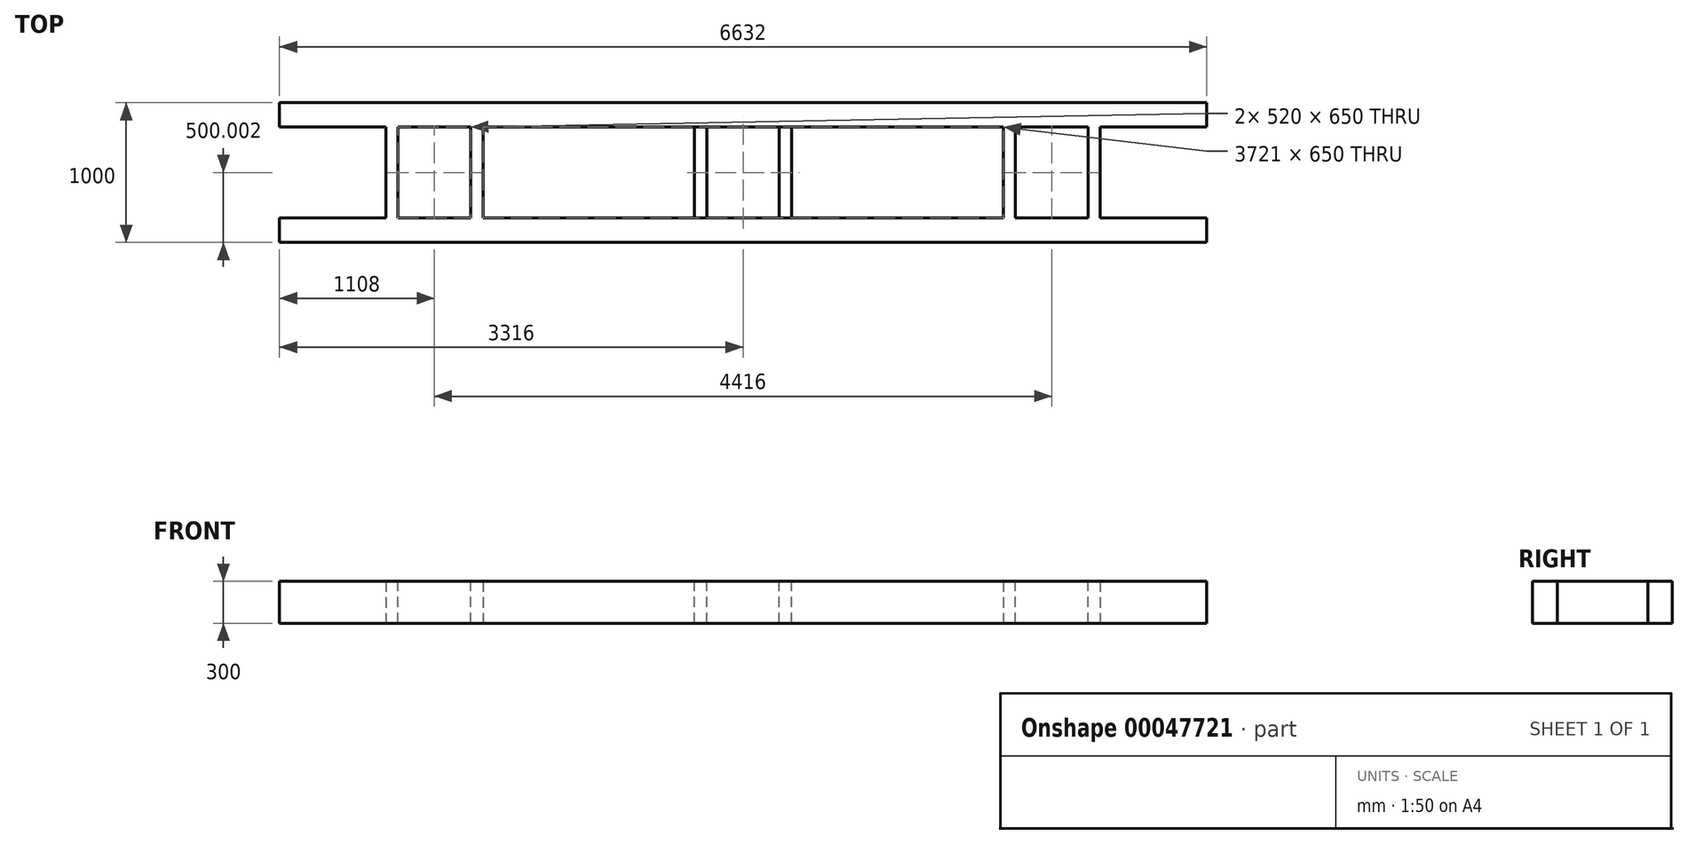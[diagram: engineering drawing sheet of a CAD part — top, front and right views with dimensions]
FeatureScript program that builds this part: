
annotation { "Feature Type Name" : "Feature", "Feature Type Description" : "" }
export const myFeature = defineFeature(function(context is Context, id is Id, definition is map)
    precondition{}
    {
        {
            var Q0;
            Q0=qCreatedBy(makeId("Top.planeOp"),FACE);
            var sketch = newSketch(context, id + "F0", { "sketchPlane" : qUnion([Q0])});
            skLineSegment(sketch, "E0.bottom", {"start": v(-3316.66, -990.23) * mm, "end": v(3315.34, -990.23) * mm});
            skLineSegment(sketch, "E0.top", {"start": v(-3316.66, -1165.23) * mm, "end": v(3315.34, -1165.23) * mm});
            skLineSegment(sketch, "E0.left", {"start": v(-3316.66, -990.23) * mm, "end": v(-3316.66, -1165.23) * mm});
            skLineSegment(sketch, "E0.right", {"start": v(3315.34, -990.23) * mm, "end": v(3315.34, -1165.23) * mm});
            skLineSegment(sketch, "E1", {"start": v(-3316.66, -990.23) * mm, "end": v(-3316.66, -340.23) * mm, "construction": true});
            skLineSegment(sketch, "E2.bottom", {"start": v(-3316.66, -340.23) * mm, "end": v(3315.34, -340.23) * mm});
            skLineSegment(sketch, "E2.top", {"start": v(-3316.66, -165.23) * mm, "end": v(3315.34, -165.23) * mm});
            skLineSegment(sketch, "E2.left", {"start": v(-3316.66, -340.23) * mm, "end": v(-3316.66, -165.23) * mm});
            skLineSegment(sketch, "E2.right", {"start": v(3315.34, -340.23) * mm, "end": v(3315.34, -165.23) * mm});
            skLineSegment(sketch, "E3.bottom", {"start": v(-3316.66, -340.23) * mm, "end": v(-2556.16, -340.23) * mm, "construction": true});
            skLineSegment(sketch, "E3.top", {"start": v(-3316.66, -990.23) * mm, "end": v(-2556.16, -990.23) * mm, "construction": true});
            skLineSegment(sketch, "E3.left", {"start": v(-3316.66, -340.23) * mm, "end": v(-3316.66, -990.23) * mm, "construction": true});
            skLineSegment(sketch, "E3.right", {"start": v(-2556.16, -340.23) * mm, "end": v(-2556.16, -990.23) * mm, "construction": true});
            skLineSegment(sketch, "E4.bottom", {"start": v(-2556.16, -340.23) * mm, "end": v(-1861.16, -340.23) * mm});
            skLineSegment(sketch, "E4.top", {"start": v(-2556.16, -990.23) * mm, "end": v(-1861.16, -990.23) * mm});
            skLineSegment(sketch, "E4.left", {"start": v(-2556.16, -340.23) * mm, "end": v(-2556.16, -990.23) * mm});
            skLineSegment(sketch, "E4.right", {"start": v(-1861.16, -340.23) * mm, "end": v(-1861.16, -990.23) * mm});
            skLineSegment(sketch, "E5.bottom", {"start": v(-2556.16, -340.23) * mm, "end": v(-348.16, -340.23) * mm, "construction": true});
            skLineSegment(sketch, "E5.top", {"start": v(-2556.16, -990.23) * mm, "end": v(-348.16, -990.23) * mm, "construction": true});
            skLineSegment(sketch, "E5.right", {"start": v(-348.16, -340.23) * mm, "end": v(-348.16, -990.23) * mm, "construction": true});
            skLineSegment(sketch, "E6.bottom", {"start": v(-348.16, -340.23) * mm, "end": v(346.84, -340.23) * mm});
            skLineSegment(sketch, "E6.top", {"start": v(-348.16, -990.23) * mm, "end": v(346.84, -990.23) * mm});
            skLineSegment(sketch, "E6.left", {"start": v(-348.16, -340.23) * mm, "end": v(-348.16, -990.23) * mm});
            skLineSegment(sketch, "E6.right", {"start": v(346.84, -340.23) * mm, "end": v(346.84, -990.23) * mm});
            skLineSegment(sketch, "E7.bottom", {"start": v(-348.16, -340.23) * mm, "end": v(1859.84, -340.23) * mm, "construction": true});
            skLineSegment(sketch, "E7.top", {"start": v(-348.16, -990.23) * mm, "end": v(1859.84, -990.23) * mm, "construction": true});
            skLineSegment(sketch, "E7.right", {"start": v(1859.84, -340.23) * mm, "end": v(1859.84, -990.23) * mm, "construction": true});
            skLineSegment(sketch, "E8.bottom", {"start": v(1859.84, -340.23) * mm, "end": v(2554.84, -340.23) * mm});
            skLineSegment(sketch, "E8.top", {"start": v(1859.84, -990.23) * mm, "end": v(2554.84, -990.23) * mm});
            skLineSegment(sketch, "E8.left", {"start": v(1859.84, -340.23) * mm, "end": v(1859.84, -990.23) * mm});
            skLineSegment(sketch, "E8.right", {"start": v(2554.84, -340.23) * mm, "end": v(2554.84, -990.23) * mm});
            skSolve(sketch);
        }
        {
            var Q0;
            Q0 = qSketchRegion(id + "F0", true);
            extrude(context, id + "F1", {"entities" : qUnion([Q0]), "depth" : 300 * mm});
        }
        {
            var Q0;
            Q0=makeQuery(id+"F1.opExtrude","CAP_FACE",FACE,{"disambiguationData":[OSD([sQuery(id+"F0.wireOp",EDGE,"E0.bottom"),sQuery(id+"F0.wireOp",EDGE,"E0.top"),sQuery(id+"F0.wireOp",EDGE,"E0.left"),sQuery(id+"F0.wireOp",EDGE,"E0.right"),sQuery(id+"F0.wireOp",EDGE,"E2.bottom"),sQuery(id+"F0.wireOp",EDGE,"E2.top"),sQuery(id+"F0.wireOp",EDGE,"E2.left"),sQuery(id+"F0.wireOp",EDGE,"E2.right"),sQuery(id+"F0.wireOp",EDGE,"E4.left"),sQuery(id+"F0.wireOp",EDGE,"E4.right"),sQuery(id+"F0.wireOp",EDGE,"E6.bottom"),sQuery(id+"F0.wireOp",EDGE,"E6.top"),sQuery(id+"F0.wireOp",EDGE,"E8.left"),sQuery(id+"F0.wireOp",EDGE,"E8.right")])],"isStart":false});
            var sketch = newSketch(context, id + "F2", { "sketchPlane" : qUnion([Q0])});
            skLineSegment(sketch, "E9", {"start": v(-2556.16, -340.23) * mm, "end": v(-1861.16, -340.23) * mm, "construction": true});
            skLineSegment(sketch, "E10", {"start": v(-1861.16, -340.23) * mm, "end": v(1859.84, -340.23) * mm, "construction": true});
            skLineSegment(sketch, "E11", {"start": v(1859.84, -340.23) * mm, "end": v(2554.84, -340.23) * mm, "construction": true});
            skLineSegment(sketch, "E12", {"start": v(-2556.16, -990.23) * mm, "end": v(-1861.16, -990.23) * mm, "construction": true});
            skLineSegment(sketch, "E13", {"start": v(1859.84, -990.23) * mm, "end": v(2554.84, -990.23) * mm, "construction": true});
            skLineSegment(sketch, "E14.bottom", {"start": v(-2556.16, -340.23) * mm, "end": v(-2468.66, -340.23) * mm, "construction": true});
            skLineSegment(sketch, "E14.top", {"start": v(-2556.16, -990.23) * mm, "end": v(-2468.66, -990.23) * mm, "construction": true});
            skLineSegment(sketch, "E14.left", {"start": v(-2556.16, -340.23) * mm, "end": v(-2556.16, -990.23) * mm, "construction": true});
            skLineSegment(sketch, "E14.right", {"start": v(-2468.66, -340.23) * mm, "end": v(-2468.66, -990.23) * mm, "construction": true});
            skLineSegment(sketch, "E15.bottom", {"start": v(-2468.66, -340.23) * mm, "end": v(-1948.66, -340.23) * mm});
            skLineSegment(sketch, "E15.top", {"start": v(-2468.66, -990.23) * mm, "end": v(-1948.66, -990.23) * mm});
            skLineSegment(sketch, "E15.left", {"start": v(-2468.66, -340.23) * mm, "end": v(-2468.66, -990.23) * mm});
            skLineSegment(sketch, "E15.right", {"start": v(-1948.66, -340.23) * mm, "end": v(-1948.66, -990.23) * mm});
            skLineSegment(sketch, "E16.bottom", {"start": v(1859.84, -340.23) * mm, "end": v(1947.34, -340.23) * mm, "construction": true});
            skLineSegment(sketch, "E16.top", {"start": v(1859.84, -990.23) * mm, "end": v(1947.34, -990.23) * mm, "construction": true});
            skLineSegment(sketch, "E16.left", {"start": v(1859.84, -340.23) * mm, "end": v(1859.84, -990.23) * mm, "construction": true});
            skLineSegment(sketch, "E16.right", {"start": v(1947.34, -340.23) * mm, "end": v(1947.34, -990.23) * mm, "construction": true});
            skLineSegment(sketch, "E17.bottom", {"start": v(2554.84, -340.23) * mm, "end": v(2467.34, -340.23) * mm, "construction": true});
            skLineSegment(sketch, "E17.top", {"start": v(2554.84, -990.23) * mm, "end": v(2467.34, -990.23) * mm, "construction": true});
            skLineSegment(sketch, "E17.left", {"start": v(2554.84, -340.23) * mm, "end": v(2554.84, -990.23) * mm, "construction": true});
            skLineSegment(sketch, "E17.right", {"start": v(2467.34, -340.23) * mm, "end": v(2467.34, -990.23) * mm, "construction": true});
            skLineSegment(sketch, "E18.bottom", {"start": v(1947.34, -340.23) * mm, "end": v(2467.34, -340.23) * mm});
            skLineSegment(sketch, "E18.top", {"start": v(1947.34, -990.23) * mm, "end": v(2467.34, -990.23) * mm});
            skLineSegment(sketch, "E18.left", {"start": v(1947.34, -340.23) * mm, "end": v(1947.34, -990.23) * mm});
            skLineSegment(sketch, "E18.right", {"start": v(2467.34, -340.23) * mm, "end": v(2467.34, -990.23) * mm});
            skSolve(sketch);
        }
        {
            var Q0;
            Q0 = qSketchRegion(id + "F2", true);
            extrude(context, id + "F3", {"entities" : qUnion([Q0]), "operationType" : NewBodyOperationType.REMOVE, "endBound" : BoundingType.THROUGH_ALL, "oppositeDirection" : true, "depth" : 25 * mm});
        }
        {
            var Q0;
            Q0=makeQuery(id+"F1.opExtrude","CAP_FACE",FACE,{"disambiguationData":[OSD([sQuery(id+"F0.wireOp",EDGE,"E0.bottom"),sQuery(id+"F0.wireOp",EDGE,"E0.top"),sQuery(id+"F0.wireOp",EDGE,"E0.left"),sQuery(id+"F0.wireOp",EDGE,"E0.right"),sQuery(id+"F0.wireOp",EDGE,"E2.bottom"),sQuery(id+"F0.wireOp",EDGE,"E2.top"),sQuery(id+"F0.wireOp",EDGE,"E2.left"),sQuery(id+"F0.wireOp",EDGE,"E2.right"),sQuery(id+"F0.wireOp",EDGE,"E4.left"),sQuery(id+"F0.wireOp",EDGE,"E4.right"),sQuery(id+"F0.wireOp",EDGE,"E6.bottom"),sQuery(id+"F0.wireOp",EDGE,"E6.top"),sQuery(id+"F0.wireOp",EDGE,"E8.left"),sQuery(id+"F0.wireOp",EDGE,"E8.right")])],"isStart":false});
            var sketch = newSketch(context, id + "F4", { "sketchPlane" : qUnion([Q0])});
            skLineSegment(sketch, "E19.bottom", {"start": v(-2556.16, -340.23) * mm, "end": v(-348.16, -340.23) * mm, "construction": true});
            skLineSegment(sketch, "E19.top", {"start": v(-2556.16, -990.23) * mm, "end": v(-348.16, -990.23) * mm, "construction": true});
            skLineSegment(sketch, "E19.left", {"start": v(-2556.16, -340.23) * mm, "end": v(-2556.16, -990.23) * mm, "construction": true});
            skLineSegment(sketch, "E19.right", {"start": v(-348.16, -340.23) * mm, "end": v(-348.16, -990.23) * mm, "construction": true});
            skLineSegment(sketch, "E20.bottom", {"start": v(-348.16, -340.23) * mm, "end": v(346.84, -340.23) * mm});
            skLineSegment(sketch, "E20.top", {"start": v(-348.16, -990.23) * mm, "end": v(346.84, -990.23) * mm});
            skLineSegment(sketch, "E20.left", {"start": v(-348.16, -340.23) * mm, "end": v(-348.16, -990.23) * mm});
            skLineSegment(sketch, "E20.right", {"start": v(346.84, -340.23) * mm, "end": v(346.84, -990.23) * mm});
            skSolve(sketch);
        }
        {
            var Q0;
            Q0 = qSketchRegion(id + "F4", true);
            extrude(context, id + "F5", {"entities" : qUnion([Q0]), "oppositeDirection" : true, "depth" : 300 * mm});
        }
        {
            var Q0;
            Q0=makeQuery(id+"F5.opExtrude","CAP_FACE",FACE,{"disambiguationData":[OSD([sQuery(id+"F4.wireOp",EDGE,"E20.bottom"),sQuery(id+"F4.wireOp",EDGE,"E20.top"),sQuery(id+"F4.wireOp",EDGE,"E20.left"),sQuery(id+"F4.wireOp",EDGE,"E20.right")])],"isStart":true});
            var sketch = newSketch(context, id + "F6", { "sketchPlane" : qUnion([Q0])});
            skLineSegment(sketch, "E21.bottom", {"start": v(-348.16, -340.23) * mm, "end": v(-260.66, -340.23) * mm, "construction": true});
            skLineSegment(sketch, "E21.top", {"start": v(-348.16, -990.23) * mm, "end": v(-260.66, -990.23) * mm, "construction": true});
            skLineSegment(sketch, "E21.left", {"start": v(-348.16, -340.23) * mm, "end": v(-348.16, -990.23) * mm, "construction": true});
            skLineSegment(sketch, "E21.right", {"start": v(-260.66, -340.23) * mm, "end": v(-260.66, -990.23) * mm, "construction": true});
            skLineSegment(sketch, "E22.bottom", {"start": v(346.84, -340.23) * mm, "end": v(259.34, -340.23) * mm, "construction": true});
            skLineSegment(sketch, "E22.top", {"start": v(346.84, -990.23) * mm, "end": v(259.34, -990.23) * mm, "construction": true});
            skLineSegment(sketch, "E22.left", {"start": v(346.84, -340.23) * mm, "end": v(346.84, -990.23) * mm, "construction": true});
            skLineSegment(sketch, "E22.right", {"start": v(259.34, -340.23) * mm, "end": v(259.34, -990.23) * mm, "construction": true});
            skLineSegment(sketch, "E23.bottom", {"start": v(-260.66, -340.23) * mm, "end": v(259.34, -340.23) * mm});
            skLineSegment(sketch, "E23.top", {"start": v(-260.66, -990.23) * mm, "end": v(259.34, -990.23) * mm});
            skLineSegment(sketch, "E23.left", {"start": v(-260.66, -340.23) * mm, "end": v(-260.66, -990.23) * mm});
            skLineSegment(sketch, "E23.right", {"start": v(259.34, -340.23) * mm, "end": v(259.34, -990.23) * mm});
            skSolve(sketch);
        }
        {
            var Q0;
            Q0 = qSketchRegion(id + "F6", true);
            extrude(context, id + "F7", {"entities" : qUnion([Q0]), "operationType" : NewBodyOperationType.REMOVE, "endBound" : BoundingType.THROUGH_ALL, "oppositeDirection" : true, "depth" : 25 * mm});
        }
    });
